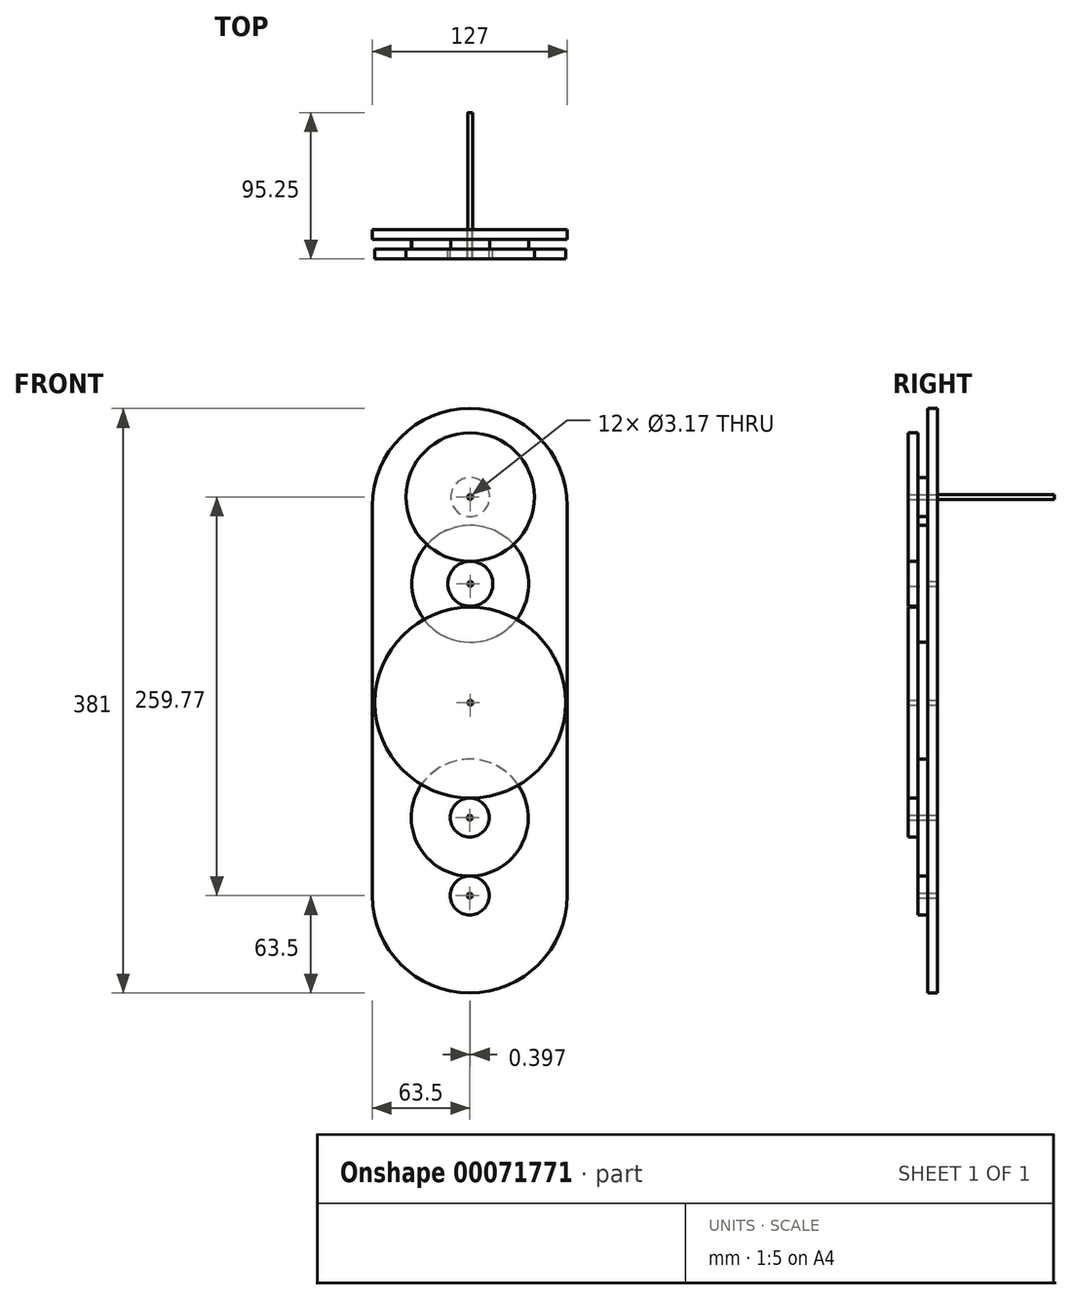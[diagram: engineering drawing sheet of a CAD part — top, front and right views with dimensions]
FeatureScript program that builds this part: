
annotation { "Feature Type Name" : "Feature", "Feature Type Description" : "" }
export const myFeature = defineFeature(function(context is Context, id is Id, definition is map)
    precondition{}
    {
        {
            var Q0;
            Q0=qCreatedBy(makeId("Front.planeOp"),FACE);
            var sketch = newSketch(context, id + "F0", { "sketchPlane" : qUnion([Q0])});
            skLineSegment(sketch, "E0.bottom", {"start": v(0, 0) * mm, "end": v(127, 0) * mm});
            skLineSegment(sketch, "E0.top", {"start": v(0, 254) * mm, "end": v(127, 254) * mm});
            skLineSegment(sketch, "E0.left", {"start": v(0, 0) * mm, "end": v(0, 254) * mm});
            skLineSegment(sketch, "E0.right", {"start": v(127, 0) * mm, "end": v(127, 254) * mm});
            skArc(sketch, "E1", {"start": v(127, 254) * mm, "mid": v(63.5, 317.5) * mm, "end": v(0, 254) * mm});
            skArc(sketch, "E2", {"start": v(0, 0) * mm, "mid": v(63.5, -63.5) * mm, "end": v(127, 0) * mm});
            skSolve(sketch);
        }
        {
            var Q0;
            Q0=makeQuery(id+"F0.imprint","IMPRINT",FACE,{"disambiguationData":[TD([[makeQuery(id+"F0.imprint","IMPRINT",EDGE,{"derivedFrom":sQuery(id+"F0.wireOp",EDGE,"E0.bottom")}),1.0]])]});
            var Q1;
            Q1=makeQuery(id+"F0.imprint","IMPRINT",FACE,{"disambiguationData":[TD([[makeQuery(id+"F0.imprint","IMPRINT",EDGE,{"derivedFrom":sQuery(id+"F0.wireOp",EDGE,"E0.top")}),1.0]])]});
            var Q2;
            Q2=makeQuery(id+"F0.imprint","IMPRINT",FACE,{"disambiguationData":[TD([[makeQuery(id+"F0.imprint","IMPRINT",EDGE,{"derivedFrom":sQuery(id+"F0.wireOp",EDGE,"E0.bottom")}),-1.0]])]});
            extrude(context, id + "F1", {"entities" : qUnion([Q0, Q1, Q2]), "depth" : 6.35 * mm});
        }
        {
            var Q0;
            Q0=makeQuery(id+"F1.opExtrude","CAP_FACE",FACE,{"disambiguationData":[OSD([sQuery(id+"F0.wireOp",EDGE,"E0.left"),sQuery(id+"F0.wireOp",EDGE,"E0.right"),sQuery(id+"F0.wireOp",EDGE,"E1"),sQuery(id+"F0.wireOp",EDGE,"E2")])],"isStart":false});
            var sketch = newSketch(context, id + "F2", { "sketchPlane" : qUnion([Q0])});
            skCircle(sketch, "E3", {"center": v(63.5, 0) * mm, "radius": 12.7 * mm});
            skCircle(sketch, "E4", {"center": v(63.5, 50.8) * mm, "radius": 38.1 * mm});
            skCircle(sketch, "E5", {"center": v(63.5, 127) * mm, "radius": 38.1 * mm});
            skLineSegment(sketch, "E6", {"start": v(63.5, 50.8) * mm, "end": v(63.5, 0) * mm, "construction": true});
            skSolve(sketch);
        }
        {
            var Q0;
            {var subQ2=sQuery(id+"F2.wireOp",EDGE,"E3");Q0=makeQuery(id+"F2.imprint","IMPRINT",FACE,{"disambiguationData":[TD([[makeQuery(id+"F2.imprint","IMPRINT",EDGE,{"derivedFrom":subQ2}),-1.0]])]});}
            var sketch = newSketch(context, id + "F3", { "sketchPlane" : qUnion([Q0])});
            skCircle(sketch, "E7", {"center": v(63.9, 125.7) * mm, "radius": 12.7 * mm});
            skCircle(sketch, "E8", {"center": v(63.9, 203.2) * mm, "radius": 38.1 * mm});
            skCircle(sketch, "E9.0", {"center": v(63.5, 127) * mm, "radius": 38.1 * mm});
            skSolve(sketch);
        }
        {
            var Q0;
            {var subQ0=sQuery(id+"F2.wireOp",EDGE,"E4");var subQ1=makeQuery(id+"F2.imprint","INTERSECT",VERTEX,{"derivedFrom":[sQuery(id+"F2.wireOp",EDGE,"E3"),subQ0]});Q0=makeQuery(id+"F2.imprint","IMPRINT",FACE,{"disambiguationData":[TD([[makeQuery(id+"F2.imprint","IMPRINT",EDGE,{"disambiguationData":[TD([[subQ1,1.0]])],"derivedFrom":subQ0}),1.0]])]});}
            var Q1;
            Q1=makeQuery(id+"F2.imprint","IMPRINT",FACE,{"disambiguationData":[TD([[makeQuery(id+"F2.imprint","IMPRINT",EDGE,{"derivedFrom":sQuery(id+"F2.wireOp",EDGE,"E3")}),1.0]])]});
            extrude(context, id + "F4", {"entities" : qUnion([Q0, Q1]), "depth" : 6.35 * mm});
        }
        {
            var Q0;
            Q0=makeQuery(id+"F4.opExtrude","CAP_FACE",FACE,{"disambiguationData":[OSD([sQuery(id+"F2.wireOp",EDGE,"E4")])],"isStart":false});
            var sketch = newSketch(context, id + "F5", { "sketchPlane" : qUnion([Q0])});
            skCircle(sketch, "E10.0", {"center": v(63.5, 50.8) * mm, "radius": 38.1 * mm, "construction": true});
            skCircle(sketch, "E11", {"center": v(63.5, 50.8) * mm, "radius": 12.7 * mm});
            skSolve(sketch);
        }
        {
            var Q0;
            Q0=makeQuery(id+"F5.imprint","IMPRINT",FACE,{"disambiguationData":[TD([[makeQuery(id+"F5.imprint","IMPRINT",EDGE,{"derivedFrom":sQuery(id+"F5.wireOp",EDGE,"E11")}),1.0]])]});
            extrude(context, id + "F6", {"entities" : qUnion([Q0]), "depth" : 6.35 * mm});
        }
        {
            var Q0;
            Q0=makeQuery(id+"F4.opExtrude","CAP_FACE",FACE,{"disambiguationData":[OSD([sQuery(id+"F2.wireOp",EDGE,"E4")])],"isStart":false});
            var sketch = newSketch(context, id + "F7", { "sketchPlane" : qUnion([Q0])});
            skCircle(sketch, "E12.0", {"center": v(63.5, 50.8) * mm, "radius": 12.7 * mm, "construction": true});
            skLineSegment(sketch, "E13", {"start": v(63.5, 50.8) * mm, "end": v(63.5, 101.6) * mm, "construction": true});
            skCircle(sketch, "E14.0", {"center": v(63.9, 125.7) * mm, "radius": 12.7 * mm, "construction": true});
            skCircle(sketch, "E15", {"center": v(63.9, 125.7) * mm, "radius": 62.2 * mm});
            skSolve(sketch);
        }
        {
            var Q0;
            {var subQ0=sQuery(id+"F7.wireOp",EDGE,"E15");var subQ1=makeQuery(id+"F4.opExtrude","CAP_EDGE",EDGE,{"disambiguationData":[OSD([sQuery(id+"F2.wireOp",EDGE,"E4")])],"isStart":false});var subQ2=makeQuery(id+"F7.imprint","INTERSECT",VERTEX,{"disambiguationData":[OD(0.0)],"derivedFrom":[subQ1,subQ0]});Q0=makeQuery(id+"F7.imprint","IMPRINT",FACE,{"disambiguationData":[TD([[makeQuery(id+"F7.imprint","IMPRINT",EDGE,{"disambiguationData":[TD([[subQ2,1.0]])],"derivedFrom":subQ0}),1.0]])]});}
            var Q1;
            {var subQ0=sQuery(id+"F7.wireOp",EDGE,"E15");var subQ1=makeQuery(id+"F4.opExtrude","CAP_EDGE",EDGE,{"disambiguationData":[OSD([sQuery(id+"F2.wireOp",EDGE,"E4")])],"isStart":false});var subQ2=makeQuery(id+"F7.imprint","INTERSECT",VERTEX,{"disambiguationData":[OD(0.0)],"derivedFrom":[subQ1,subQ0]});Q1=makeQuery(id+"F7.imprint","IMPRINT",FACE,{"disambiguationData":[TD([[makeQuery(id+"F7.imprint","IMPRINT",EDGE,{"disambiguationData":[TD([[subQ2,-1.0]])],"derivedFrom":subQ0}),1.0]])]});}
            extrude(context, id + "F8", {"entities" : qUnion([Q0, Q1]), "depth" : 6.35 * mm});
        }
        {
            var Q0;
            Q0=sQuery(id+"F2.wireOp",EDGE,"E5");
            extrude(context, id + "F9", {"bodyType" : ToolBodyType.SURFACE, "surfaceEntities" : qUnion([Q0]), "depth" : 6.35 * mm});
        }
        {
            var Q0;
            Q0=makeQuery(id+"F3.imprint","IMPRINT",FACE,{"disambiguationData":[TD([[makeQuery(id+"F3.imprint","IMPRINT",EDGE,{"derivedFrom":sQuery(id+"F3.wireOp",EDGE,"E8")}),1.0]])]});
            extrude(context, id + "F10", {"entities" : qUnion([Q0]), "depth" : 6.35 * mm});
        }
        {
            var Q0;
            Q0=makeQuery(id+"F10.opExtrude","CAP_FACE",FACE,{"disambiguationData":[OSD([sQuery(id+"F3.wireOp",EDGE,"E8")])],"isStart":false});
            var sketch = newSketch(context, id + "F11", { "sketchPlane" : qUnion([Q0])});
            skCircle(sketch, "E16", {"center": v(63.9, 203.2) * mm, "radius": 14.68 * mm});
            skSolve(sketch);
        }
        {
            var Q0;
            Q0=makeQuery(id+"F11.imprint","IMPRINT",FACE,{"disambiguationData":[TD([[makeQuery(id+"F11.imprint","IMPRINT",EDGE,{"derivedFrom":sQuery(id+"F11.wireOp",EDGE,"E16")}),1.0]])]});
            extrude(context, id + "F12", {"entities" : qUnion([Q0]), "operationType" : NewBodyOperationType.ADD, "depth" : 6.35 * mm});
        }
        {
            var Q0;
            {var subQ2=sQuery(id+"F2.wireOp",EDGE,"E3");Q0=makeQuery(id+"F2.imprint","IMPRINT",FACE,{"disambiguationData":[TD([[makeQuery(id+"F2.imprint","IMPRINT",EDGE,{"derivedFrom":subQ2}),-1.0]])]});}
            var sketch = newSketch(context, id + "F13", { "sketchPlane" : qUnion([Q0])});
            skLineSegment(sketch, "E17", {"start": v(0, 259.77) * mm, "end": v(127.55, 259.77) * mm});
            skCircle(sketch, "E18", {"center": v(63.78, 259.77) * mm, "radius": 12.72 * mm});
            skSolve(sketch);
        }
        {
            var Q0;
            Q0 = qSketchRegion(id + "F13", true);
            extrude(context, id + "F14", {"entities" : qUnion([Q0]), "depth" : 6.35 * mm});
        }
        {
            var Q0;
            Q0=makeQuery(id+"F14.opExtrude","CAP_FACE",FACE,{"disambiguationData":[OSD([sQuery(id+"F13.wireOp",EDGE,"E18")])],"isStart":false});
            var sketch = newSketch(context, id + "F15", { "sketchPlane" : qUnion([Q0])});
            skCircle(sketch, "E19", {"center": v(63.78, 259.77) * mm, "radius": 41.89 * mm});
            skCircle(sketch, "E20.0", {"center": v(63.9, 203.2) * mm, "radius": 14.68 * mm, "construction": true});
            skSolve(sketch);
        }
        {
            var Q0;
            Q0 = qSketchRegion(id + "F15", true);
            extrude(context, id + "F16", {"entities" : qUnion([Q0]), "depth" : 6.35 * mm});
        }
        {
            var Q0;
            Q0=makeQuery(id+"F1.opExtrude","CAP_FACE",FACE,{"disambiguationData":[OSD([sQuery(id+"F0.wireOp",EDGE,"E0.left"),sQuery(id+"F0.wireOp",EDGE,"E0.right"),sQuery(id+"F0.wireOp",EDGE,"E1"),sQuery(id+"F0.wireOp",EDGE,"E2")])],"isStart":true});
            var sketch = newSketch(context, id + "F17", { "sketchPlane" : qUnion([Q0])});
            skCircle(sketch, "E21.0", {"center": v(-63.78, 259.77) * mm, "radius": 41.89 * mm});
            skCircle(sketch, "E22.0", {"center": v(-63.9, 203.2) * mm, "radius": 14.68 * mm});
            skCircle(sketch, "E23.0", {"center": v(-63.9, 125.7) * mm, "radius": 62.2 * mm});
            skCircle(sketch, "E24.0", {"center": v(-63.5, 50.8) * mm, "radius": 12.7 * mm});
            skCircle(sketch, "E25.0", {"center": v(-63.5, 0) * mm, "radius": 12.7 * mm});
            skCircle(sketch, "E26", {"center": v(-63.78, 259.77) * mm, "radius": 1.59 * mm});
            skCircle(sketch, "E27", {"center": v(-63.9, 203.2) * mm, "radius": 1.59 * mm});
            skCircle(sketch, "E28", {"center": v(-63.9, 125.7) * mm, "radius": 1.59 * mm});
            skCircle(sketch, "E29", {"center": v(-63.5, 50.8) * mm, "radius": 1.59 * mm});
            skCircle(sketch, "E30", {"center": v(-63.5, 0) * mm, "radius": 1.59 * mm});
            skSolve(sketch);
        }
        {
            var Q0;
            Q0=makeQuery(id+"F17.imprint","IMPRINT",FACE,{"disambiguationData":[TD([[makeQuery(id+"F17.imprint","IMPRINT",EDGE,{"derivedFrom":sQuery(id+"F17.wireOp",EDGE,"E26")}),1.0]])]});
            var Q1;
            Q1=makeQuery(id+"F17.imprint","IMPRINT",FACE,{"disambiguationData":[TD([[makeQuery(id+"F17.imprint","IMPRINT",EDGE,{"derivedFrom":sQuery(id+"F17.wireOp",EDGE,"E27")}),1.0]])]});
            var Q2;
            Q2=makeQuery(id+"F17.imprint","IMPRINT",FACE,{"disambiguationData":[TD([[makeQuery(id+"F17.imprint","IMPRINT",EDGE,{"derivedFrom":sQuery(id+"F17.wireOp",EDGE,"E28")}),1.0]])]});
            var Q3;
            Q3=makeQuery(id+"F17.imprint","IMPRINT",FACE,{"disambiguationData":[TD([[makeQuery(id+"F17.imprint","IMPRINT",EDGE,{"derivedFrom":sQuery(id+"F17.wireOp",EDGE,"E29")}),1.0]])]});
            var Q4;
            Q4=makeQuery(id+"F17.imprint","IMPRINT",FACE,{"disambiguationData":[TD([[makeQuery(id+"F17.imprint","IMPRINT",EDGE,{"derivedFrom":sQuery(id+"F17.wireOp",EDGE,"E30")}),1.0]])]});
            extrude(context, id + "F18", {"entities" : qUnion([Q0, Q1, Q2, Q3, Q4]), "operationType" : NewBodyOperationType.REMOVE, "endBound" : BoundingType.THROUGH_ALL, "oppositeDirection" : true, "depth" : 25.4 * mm});
        }
        {
            var Q0;
            Q0=makeQuery(id+"F17.imprint","IMPRINT",FACE,{"disambiguationData":[TD([[makeQuery(id+"F17.imprint","IMPRINT",EDGE,{"derivedFrom":sQuery(id+"F17.wireOp",EDGE,"E26")}),1.0]])]});
            extrude(context, id + "F19", {"entities" : qUnion([Q0]), "depth" : 76.2 * mm});
        }
    });
